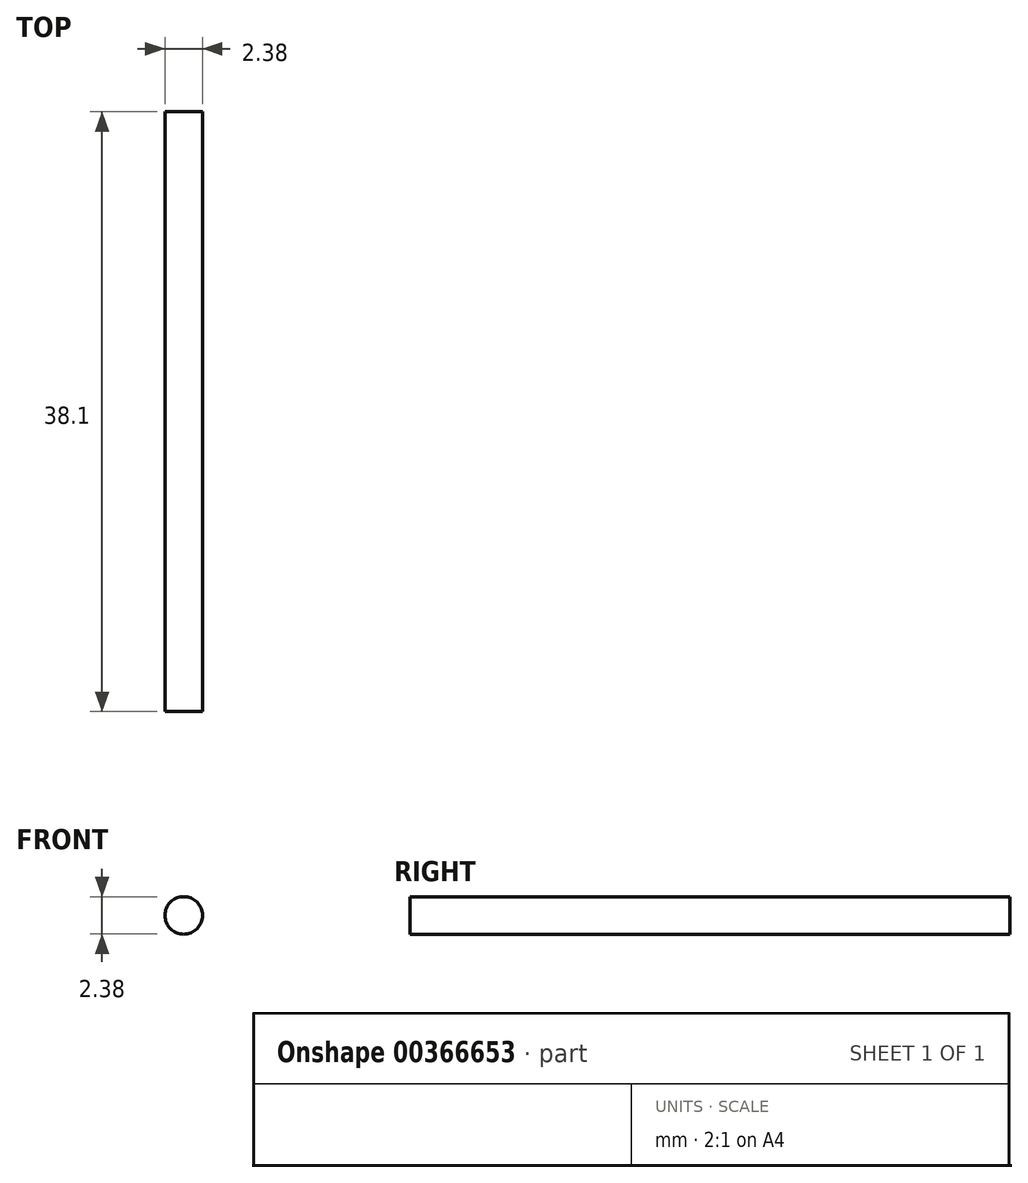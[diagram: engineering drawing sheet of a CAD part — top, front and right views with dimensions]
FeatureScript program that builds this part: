
annotation { "Feature Type Name" : "Feature", "Feature Type Description" : "" }
export const myFeature = defineFeature(function(context is Context, id is Id, definition is map)
    precondition{}
    {
        {
            var Q0;
            Q0=qCreatedBy(makeId("Front.planeOp"),FACE);
            var sketch = newSketch(context, id + "F0", { "sketchPlane" : qUnion([Q0])});
            skCircle(sketch, "E0", {"center": v(0, 0) * mm, "radius": 1.2 * mm});
            skSolve(sketch);
        }
        {
            var Q0;
            Q0=makeQuery(id+"F0.imprint","IMPRINT",FACE,{"disambiguationData":[TD([[makeQuery(id+"F0.imprint","IMPRINT",EDGE,{"derivedFrom":sQuery(id+"F0.wireOp",EDGE,"E0")}),1.0]])]});
            extrude(context, id + "F1", {"entities" : qUnion([Q0]), "depth" : 38.1 * mm});
        }
    });
